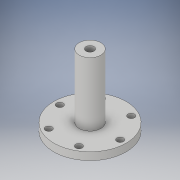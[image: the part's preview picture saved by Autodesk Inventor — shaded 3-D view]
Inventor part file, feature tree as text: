
AUTODESK INVENTOR PART (.ipt)
format: ipt  version: 2017 (Build 210142000, 142)  size: 148,992 bytes
history: native  units: in
note: dims shown in document units (in); Inventor stores cm internally (conversion verified against a paired STEP export)
features: sketch x3, revolve x1, extrude x1, hole x1, pattern_circular x1
ambient origin geometry x8: Origin, YZ Plane, XZ Plane, XY Plane, X Axis, Y Axis, Z Axis, Center Point
bodies: Solid1 (feature_tree)
feature tree (7):
  revolve  "Revolution1"  [1 undecoded]
  extrude  "Extrusion1"  TaperAngle=90.0deg  [1 undecoded]
  hole  "Hole2"  [1 undecoded]
  pattern_circular  "Circular Pattern1"  Count=6 Angle=360.0deg
  sketch  "Sketch1"  dims[d0=1.0394in d5=0.2362in]
  sketch  "Sketch4"  dims[d11=0.2096in d14=90.0deg]
  sketch  "Sketch5"  dims[d23=0.935in d24=0.2047in d25=2.3622in d27=360.0deg d29=0.2362in d30=0.0in d32=0.125in d37=1.1181in d38=1.9685in d39=0.385in d40=45.0deg d42=0.104in d43=0.2in d44=0.375in d45=0.25in d46=0.5635in d47=0.2in d48=0.8108in d49=1.5748in d50=360.0deg]
note: 3 required parameter values undecoded (feature->parameter linkage not recoverable at this tier; creation-order binding heuristic only, values carry confidence <= 0.55)